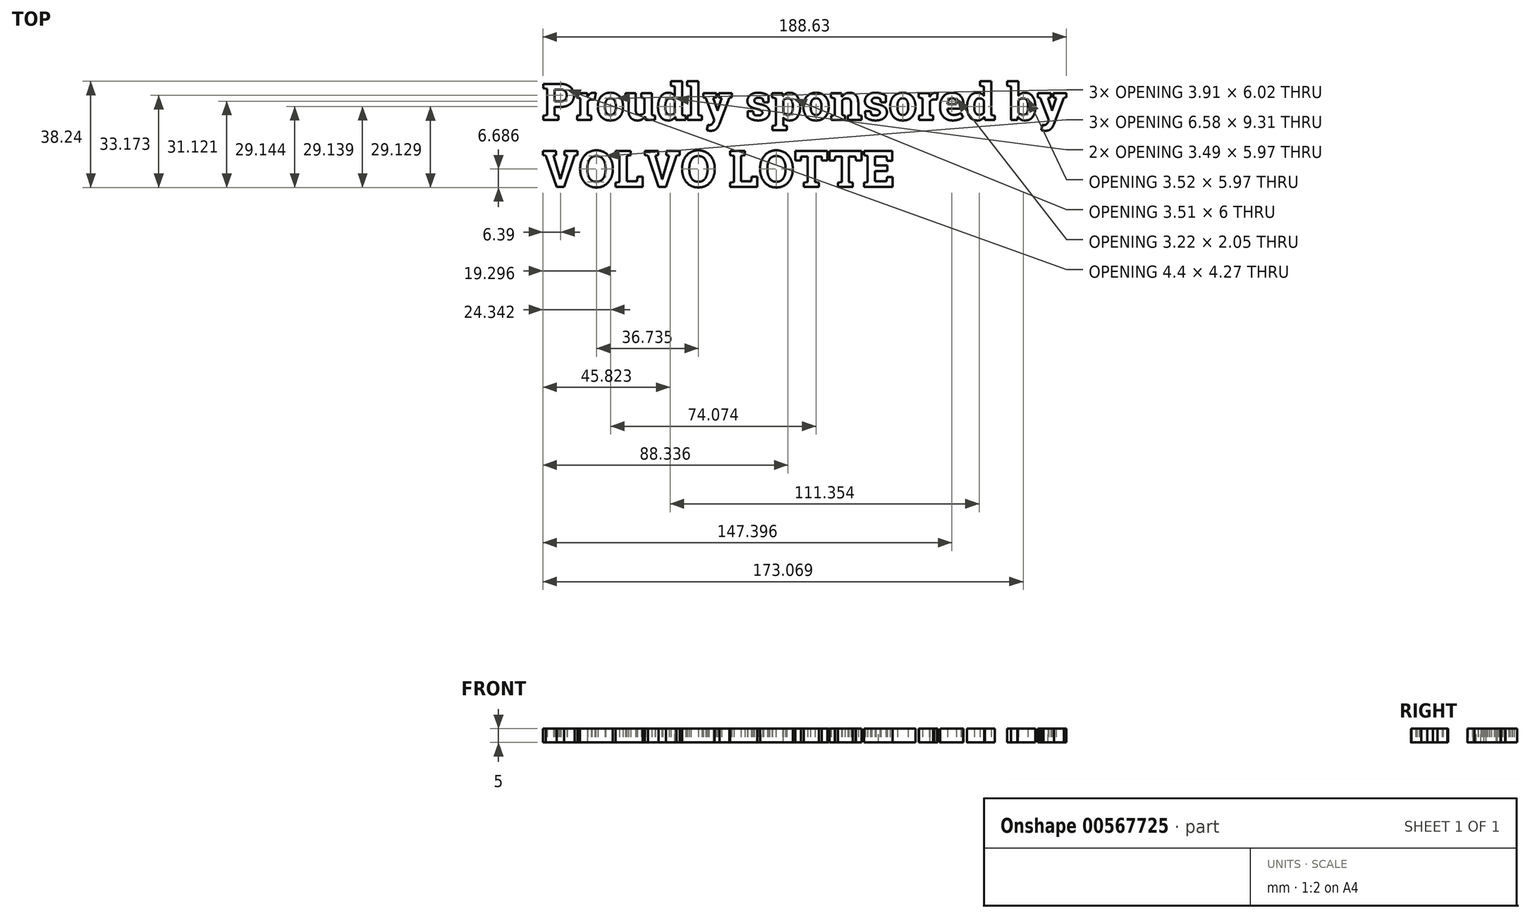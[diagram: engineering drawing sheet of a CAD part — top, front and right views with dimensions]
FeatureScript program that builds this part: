
annotation { "Feature Type Name" : "Feature", "Feature Type Description" : "" }
export const myFeature = defineFeature(function(context is Context, id is Id, definition is map)
    precondition{}
    {
        {
            var Q0;
            Q0=qCreatedBy(makeId("Top.planeOp"),FACE);
            var sketch = newSketch(context, id + "F0", { "sketchPlane" : qUnion([Q0])});
            skLineSegment(sketch, "E0.bottom", {"start": v(-100, 20) * mm, "end": v(100, 20) * mm});
            skLineSegment(sketch, "E0.top", {"start": v(-100, -20) * mm, "end": v(100, -20) * mm});
            skLineSegment(sketch, "E0.left", {"start": v(-100, 20) * mm, "end": v(-100, -20) * mm});
            skLineSegment(sketch, "E0.right", {"start": v(100, 20) * mm, "end": v(100, -20) * mm});
            skPoint(sketch, "E0.middle", {"position": v(0, 0) * mm});
            skSolve(sketch);
        }
        {
            var Q0;
            Q0 = qSketchRegion(id + "F0", true);
            extrude(context, id + "F1", {"entities" : qUnion([Q0]), "depth" : 5 * mm, "offsetDistance" : 25 * mm});
        }
        {
            var Q0;
            Q0=makeQuery(id+"F1.opExtrude","CAP_FACE",FACE,{"disambiguationData":[OSD([sQuery(id+"F0.wireOp",EDGE,"E0.bottom"),sQuery(id+"F0.wireOp",EDGE,"E0.top"),sQuery(id+"F0.wireOp",EDGE,"E0.left"),sQuery(id+"F0.wireOp",EDGE,"E0.right")])],"isStart":false});
            var sketch = newSketch(context, id + "F2", { "sketchPlane" : qUnion([Q0])});
            skText(sketch, "E1", { "text": "Proudly sponsored by \nVOLVO LOTTE", "fontName": "RobotoSlab-Bold.ttf"});
            const initialGuessF2  = {"E1": [-0.09454, 0.00484, 1, 0, 0.01316]};
            skSetInitialGuess(sketch, initialGuessF2);
            skSolve(sketch);
        }
        {
            var Q0;
            Q0 = qSketchRegion(id + "F2", true);
            extrude(context, id + "F3", {"entities" : qUnion([Q0]), "operationType" : NewBodyOperationType.ADD, "depth" : 5 * mm, "offsetDistance" : 25 * mm});
        }
        {
            var Q0;
            Q0=makeQuery(id+"F1.opExtrude","SWEPT_EDGE",EDGE,{"disambiguationData":[OSD([sQuery(id+"F0.wireOp",EDGE,"E0.bottom"),sQuery(id+"F0.wireOp",EDGE,"E0.left")])]});
            var Q1;
            Q1=makeQuery(id+"F1.opExtrude","SWEPT_EDGE",EDGE,{"disambiguationData":[OSD([sQuery(id+"F0.wireOp",EDGE,"E0.top"),sQuery(id+"F0.wireOp",EDGE,"E0.left")])]});
            var Q2;
            Q2=makeQuery(id+"F1.opExtrude","SWEPT_EDGE",EDGE,{"disambiguationData":[OSD([sQuery(id+"F0.wireOp",EDGE,"E0.top"),sQuery(id+"F0.wireOp",EDGE,"E0.right")])]});
            var Q3;
            Q3=makeQuery(id+"F1.opExtrude","SWEPT_EDGE",EDGE,{"disambiguationData":[OSD([sQuery(id+"F0.wireOp",EDGE,"E0.bottom"),sQuery(id+"F0.wireOp",EDGE,"E0.right")])]});
            fillet(context, id + "F4", {"entities" : qUnion([Q0, Q1, Q2, Q3]), "radius" : 10 * mm, "tangentPropagation" : true, "allowEdgeOverflow" : false});
        }
        {
            var Q0;
            Q0=makeQuery(id+"F1.opExtrude","CAP_FACE",FACE,{"disambiguationData":[OSD([sQuery(id+"F0.wireOp",EDGE,"E0.bottom"),sQuery(id+"F0.wireOp",EDGE,"E0.top"),sQuery(id+"F0.wireOp",EDGE,"E0.left"),sQuery(id+"F0.wireOp",EDGE,"E0.right")])],"isStart":true});
            extrude(context, id + "F5", {"entities" : qUnion([Q0]), "operationType" : NewBodyOperationType.REMOVE, "oppositeDirection" : true, "depth" : 5 * mm, "offsetDistance" : 25 * mm});
        }
    });
